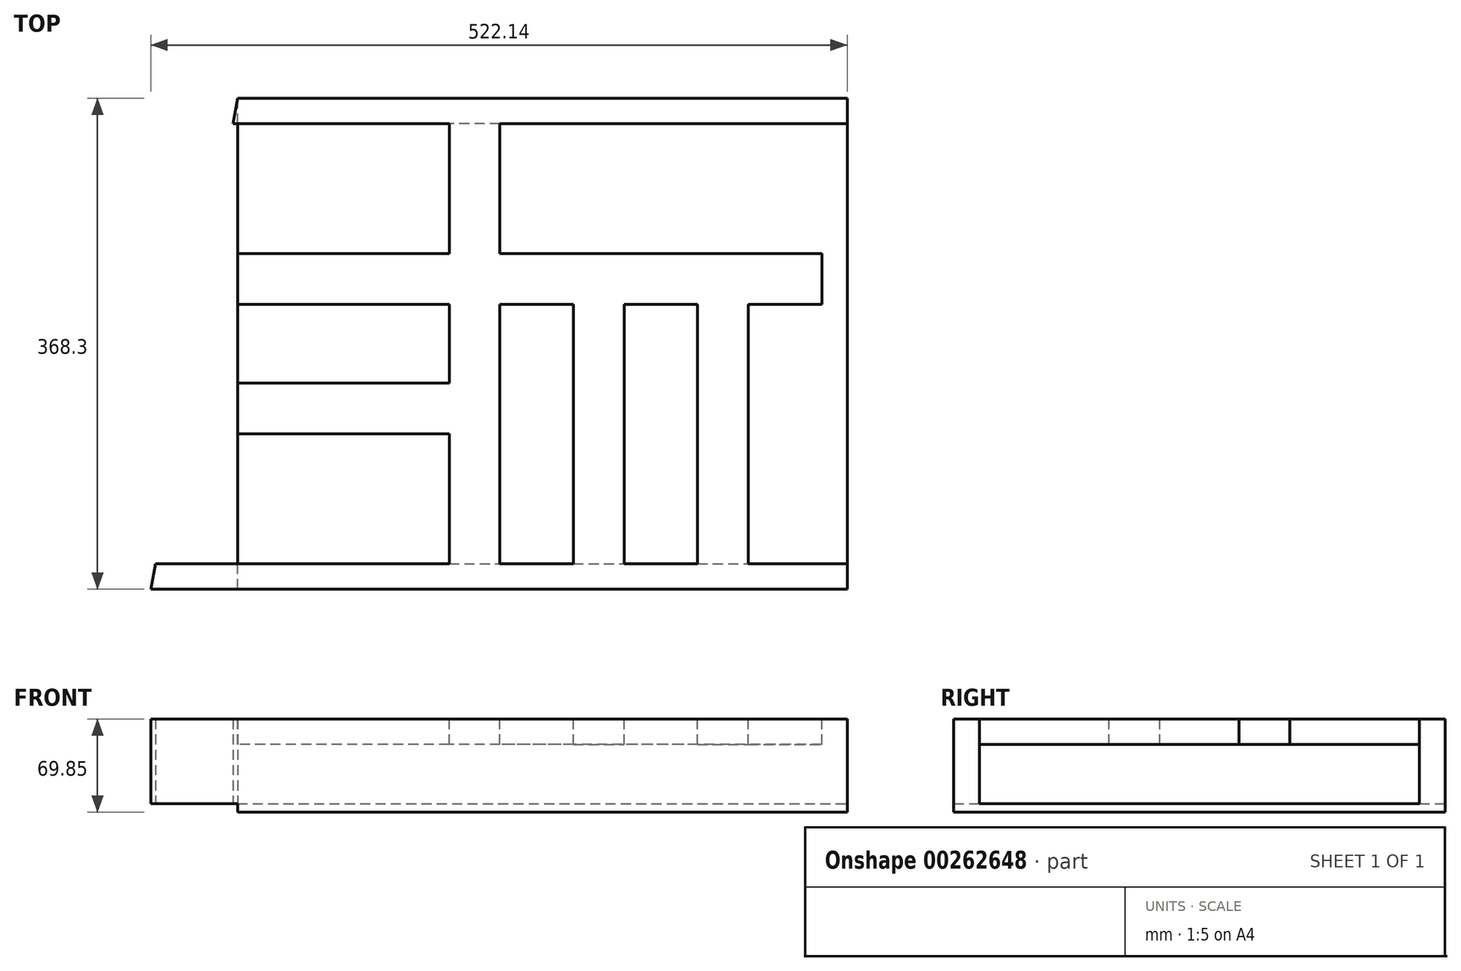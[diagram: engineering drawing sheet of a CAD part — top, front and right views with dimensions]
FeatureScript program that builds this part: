
annotation { "Feature Type Name" : "Feature", "Feature Type Description" : "" }
export const myFeature = defineFeature(function(context is Context, id is Id, definition is map)
    precondition{}
    {
        {
            var Q0;
            Q0=qCreatedBy(makeId("Top.planeOp"),FACE);
            var sketch = newSketch(context, id + "F0", { "sketchPlane" : qUnion([Q0])});
            skLineSegment(sketch, "E0.bottom", {"start": v(0, 0) * mm, "end": v(457.2, 0) * mm});
            skLineSegment(sketch, "E0.top", {"start": v(0, 368.3) * mm, "end": v(457.2, 368.3) * mm});
            skLineSegment(sketch, "E0.left", {"start": v(0, 0) * mm, "end": v(0, 368.3) * mm});
            skLineSegment(sketch, "E0.right", {"start": v(457.2, 0) * mm, "end": v(457.2, 368.3) * mm});
            skSolve(sketch);
        }
        {
            var Q0;
            Q0=makeQuery(id+"F0.imprint","IMPRINT",FACE,{"disambiguationData":[TD([[makeQuery(id+"F0.imprint","IMPRINT",EDGE,{"derivedFrom":sQuery(id+"F0.wireOp",EDGE,"E0.bottom")}),1.0]])]});
            extrude(context, id + "F1", {"entities" : qUnion([Q0]), "depth" : 6.35 * mm, "offsetDistance" : 25.4 * mm});
        }
        {
            var Q0;
            Q0=makeQuery(id+"F1.opExtrude","CAP_FACE",FACE,{"disambiguationData":[OSD([sQuery(id+"F0.wireOp",EDGE,"E0.bottom"),sQuery(id+"F0.wireOp",EDGE,"E0.top"),sQuery(id+"F0.wireOp",EDGE,"E0.left"),sQuery(id+"F0.wireOp",EDGE,"E0.right")])],"isStart":false});
            var sketch = newSketch(context, id + "F2", { "sketchPlane" : qUnion([Q0])});
            skLineSegment(sketch, "E1.bottom", {"start": v(-64.94, 0) * mm, "end": v(457.2, 0) * mm});
            skLineSegment(sketch, "E1.top", {"start": v(-61.58, 19.05) * mm, "end": v(457.2, 19.05) * mm});
            skLineSegment(sketch, "E1.right", {"start": v(457.2, 0) * mm, "end": v(457.2, 19.05) * mm});
            skLineSegment(sketch, "E2.bottom", {"start": v(0, 368.3) * mm, "end": v(457.2, 368.3) * mm});
            skLineSegment(sketch, "E2.top", {"start": v(-3.36, 349.25) * mm, "end": v(457.2, 349.25) * mm});
            skLineSegment(sketch, "E2.right", {"start": v(457.2, 368.3) * mm, "end": v(457.2, 349.25) * mm});
            skLineSegment(sketch, "E3.bottom", {"start": v(457.2, 349.25) * mm, "end": v(438.15, 349.25) * mm});
            skLineSegment(sketch, "E3.top", {"start": v(457.2, 19.05) * mm, "end": v(438.15, 19.05) * mm});
            skLineSegment(sketch, "E3.left", {"start": v(457.2, 349.25) * mm, "end": v(457.2, 19.05) * mm});
            skLineSegment(sketch, "E3.right", {"start": v(438.15, 349.25) * mm, "end": v(438.15, 19.05) * mm});
            skLineSegment(sketch, "E4", {"start": v(0, 368.3) * mm, "end": v(-3.36, 349.25) * mm});
            skLineSegment(sketch, "E5.trimOffspring", {"start": v(-61.58, 19.05) * mm, "end": v(-64.94, 0) * mm});
            skPoint(sketch, "E1.left.start.orphan", {"position": v(0, 0) * mm});
            skSolve(sketch);
        }
        {
            var Q0;
            {var subQ3=sQuery(id+"F2.wireOp",EDGE,"E5.trimOffspring");Q0=makeQuery(id+"F2.imprint","IMPRINT",FACE,{"disambiguationData":[TD([[makeQuery(id+"F2.imprint","IMPRINT",EDGE,{"derivedFrom":subQ3}),1.0]])]});}
            var Q1;
            {var subQ1=sQuery(id+"F2.wireOp",EDGE,"E1.right");Q1=makeQuery(id+"F2.imprint","IMPRINT",FACE,{"disambiguationData":[TD([[makeQuery(id+"F2.imprint","IMPRINT",EDGE,{"derivedFrom":subQ1}),1.0]])]});}
            var Q2;
            Q2=makeQuery(id+"F2.imprint","IMPRINT",FACE,{"disambiguationData":[TD([[makeQuery(id+"F2.imprint","IMPRINT",EDGE,{"derivedFrom":sQuery(id+"F2.wireOp",EDGE,"E3.bottom")}),1.0]])]});
            var Q3;
            {var subQ4=sQuery(id+"F2.wireOp",EDGE,"E2.bottom");Q3=makeQuery(id+"F2.imprint","IMPRINT",FACE,{"disambiguationData":[TD([[makeQuery(id+"F2.imprint","IMPRINT",EDGE,{"derivedFrom":subQ4}),-1.0]])]});}
            var Q4;
            {var subQ0=sQuery(id+"F2.wireOp",EDGE,"E4");Q4=makeQuery(id+"F2.imprint","IMPRINT",FACE,{"disambiguationData":[TD([[makeQuery(id+"F2.imprint","IMPRINT",EDGE,{"derivedFrom":subQ0}),1.0]])]});}
            extrude(context, id + "F3", {"entities" : qUnion([Q0, Q1, Q2, Q3, Q4]), "operationType" : NewBodyOperationType.ADD, "depth" : 63.5 * mm, "offsetDistance" : 25.4 * mm});
        }
        {
            var Q0;
            Q0=makeQuery(id+"F3.opExtrude","CAP_FACE",FACE,{"disambiguationData":[OSD([sQuery(id+"F2.wireOp",EDGE,"E1.bottom"),sQuery(id+"F2.wireOp",EDGE,"E1.top"),sQuery(id+"F2.wireOp",EDGE,"E1.left"),sQuery(id+"F2.wireOp",EDGE,"E1.right"),sQuery(id+"F2.wireOp",EDGE,"E2.bottom"),sQuery(id+"F2.wireOp",EDGE,"E2.top"),sQuery(id+"F2.wireOp",EDGE,"E2.left"),sQuery(id+"F2.wireOp",EDGE,"E2.right"),sQuery(id+"F2.wireOp",EDGE,"E3.left"),sQuery(id+"F2.wireOp",EDGE,"E3.right")])],"isStart":false});
            var sketch = newSketch(context, id + "F4", { "sketchPlane" : qUnion([Q0])});
            skLineSegment(sketch, "E6.bottom", {"start": v(383.1, 19.05) * mm, "end": v(345, 19.05) * mm});
            skLineSegment(sketch, "E6.top", {"start": v(383.1, 251.9) * mm, "end": v(345, 251.9) * mm});
            skLineSegment(sketch, "E6.left", {"start": v(383.1, 19.05) * mm, "end": v(383.1, 251.9) * mm});
            skLineSegment(sketch, "E6.right", {"start": v(345, 19.05) * mm, "end": v(345, 251.9) * mm});
            skLineSegment(sketch, "E7.left", {"start": v(289.97, 19.05) * mm, "end": v(289.97, 251.9) * mm});
            skLineSegment(sketch, "E7.right", {"start": v(251.87, 19.05) * mm, "end": v(251.87, 251.9) * mm});
            skLineSegment(sketch, "E8.bottom", {"start": v(196.85, 19.05) * mm, "end": v(158.75, 19.05) * mm});
            skLineSegment(sketch, "E8.top", {"start": v(196.85, 349.25) * mm, "end": v(158.75, 349.25) * mm});
            skLineSegment(sketch, "E8.left", {"start": v(196.85, 19.05) * mm, "end": v(196.85, 349.25) * mm});
            skLineSegment(sketch, "E8.right", {"start": v(158.75, 19.05) * mm, "end": v(158.75, 349.25) * mm});
            skLineSegment(sketch, "E9.bottom", {"start": v(383.1, 251.9) * mm, "end": v(438.15, 251.9) * mm});
            skLineSegment(sketch, "E9.top", {"start": v(383.1, 213.8) * mm, "end": v(438.15, 213.8) * mm});
            skLineSegment(sketch, "E9.left", {"start": v(383.1, 251.9) * mm, "end": v(383.1, 213.8) * mm});
            skLineSegment(sketch, "E9.right", {"start": v(438.15, 251.9) * mm, "end": v(438.15, 213.8) * mm});
            skLineSegment(sketch, "E10.bottom", {"start": v(345, 251.9) * mm, "end": v(289.97, 251.9) * mm});
            skLineSegment(sketch, "E10.top", {"start": v(345, 213.8) * mm, "end": v(289.97, 213.8) * mm});
            skLineSegment(sketch, "E10.left", {"start": v(345, 251.9) * mm, "end": v(345, 213.8) * mm});
            skLineSegment(sketch, "E10.right", {"start": v(289.97, 251.9) * mm, "end": v(289.97, 213.8) * mm});
            skLineSegment(sketch, "E11", {"start": v(289.97, 251.9) * mm, "end": v(251.87, 251.9) * mm});
            skLineSegment(sketch, "E12.bottom", {"start": v(251.87, 251.9) * mm, "end": v(196.85, 251.9) * mm});
            skLineSegment(sketch, "E12.top", {"start": v(251.87, 213.8) * mm, "end": v(196.85, 213.8) * mm});
            skLineSegment(sketch, "E12.left", {"start": v(251.87, 251.9) * mm, "end": v(251.87, 213.8) * mm});
            skLineSegment(sketch, "E12.right", {"start": v(196.85, 251.9) * mm, "end": v(196.85, 213.8) * mm});
            skLineSegment(sketch, "E13.bottom", {"start": v(158.75, 251.9) * mm, "end": v(0, 251.9) * mm});
            skLineSegment(sketch, "E13.top", {"start": v(158.75, 213.8) * mm, "end": v(0, 213.8) * mm});
            skLineSegment(sketch, "E13.left", {"start": v(158.75, 251.9) * mm, "end": v(158.75, 213.8) * mm});
            skLineSegment(sketch, "E13.right", {"start": v(0, 251.9) * mm, "end": v(0, 213.8) * mm});
            skLineSegment(sketch, "E14.bottom", {"start": v(158.75, 154.53) * mm, "end": v(0, 154.53) * mm});
            skLineSegment(sketch, "E14.top", {"start": v(158.75, 116.43) * mm, "end": v(0, 116.43) * mm});
            skLineSegment(sketch, "E14.left", {"start": v(158.75, 154.53) * mm, "end": v(158.75, 116.43) * mm});
            skLineSegment(sketch, "E14.right", {"start": v(0, 154.53) * mm, "end": v(0, 116.43) * mm});
            skLineSegment(sketch, "E15", {"start": v(289.97, 19.05) * mm, "end": v(251.87, 19.05) * mm});
            skSolve(sketch);
        }
        {
            var Q0;
            Q0=makeQuery(id+"F4.imprint","IMPRINT",FACE,{"disambiguationData":[TD([[makeQuery(id+"F4.imprint","IMPRINT",EDGE,{"derivedFrom":sQuery(id+"F4.wireOp",EDGE,"E13.bottom")}),1.0]])]});
            var Q1;
            {var subQ4=sQuery(id+"F4.wireOp",EDGE,"E8.bottom");Q1=makeQuery(id+"F4.imprint","IMPRINT",FACE,{"disambiguationData":[TD([[makeQuery(id+"F4.imprint","IMPRINT",EDGE,{"derivedFrom":subQ4}),1.0]])]});}
            var Q2;
            Q2=makeQuery(id+"F4.imprint","IMPRINT",FACE,{"disambiguationData":[TD([[makeQuery(id+"F4.imprint","IMPRINT",EDGE,{"derivedFrom":sQuery(id+"F4.wireOp",EDGE,"E12.bottom")}),1.0]])]});
            var Q3;
            Q3=makeQuery(id+"F4.imprint","IMPRINT",FACE,{"disambiguationData":[TD([[makeQuery(id+"F4.imprint","IMPRINT",EDGE,{"derivedFrom":sQuery(id+"F4.wireOp",EDGE,"E7.left")}),1.0]])]});
            var Q4;
            Q4=makeQuery(id+"F4.imprint","IMPRINT",FACE,{"disambiguationData":[TD([[makeQuery(id+"F4.imprint","IMPRINT",EDGE,{"derivedFrom":sQuery(id+"F4.wireOp",EDGE,"E10.bottom")}),1.0]])]});
            var Q5;
            Q5=makeQuery(id+"F4.imprint","IMPRINT",FACE,{"disambiguationData":[TD([[makeQuery(id+"F4.imprint","IMPRINT",EDGE,{"derivedFrom":sQuery(id+"F4.wireOp",EDGE,"E6.bottom")}),1.0]])]});
            var Q6;
            Q6=makeQuery(id+"F4.imprint","IMPRINT",FACE,{"disambiguationData":[TD([[makeQuery(id+"F4.imprint","IMPRINT",EDGE,{"derivedFrom":sQuery(id+"F4.wireOp",EDGE,"E9.bottom")}),-1.0]])]});
            var Q7;
            Q7=makeQuery(id+"F4.imprint","IMPRINT",FACE,{"disambiguationData":[TD([[makeQuery(id+"F4.imprint","IMPRINT",EDGE,{"derivedFrom":sQuery(id+"F4.wireOp",EDGE,"E14.bottom")}),1.0]])]});
            extrude(context, id + "F5", {"entities" : qUnion([Q0, Q1, Q2, Q3, Q4, Q5, Q6, Q7]), "operationType" : NewBodyOperationType.ADD, "oppositeDirection" : true, "depth" : 19.05 * mm, "offsetDistance" : 25.4 * mm});
        }
    });
